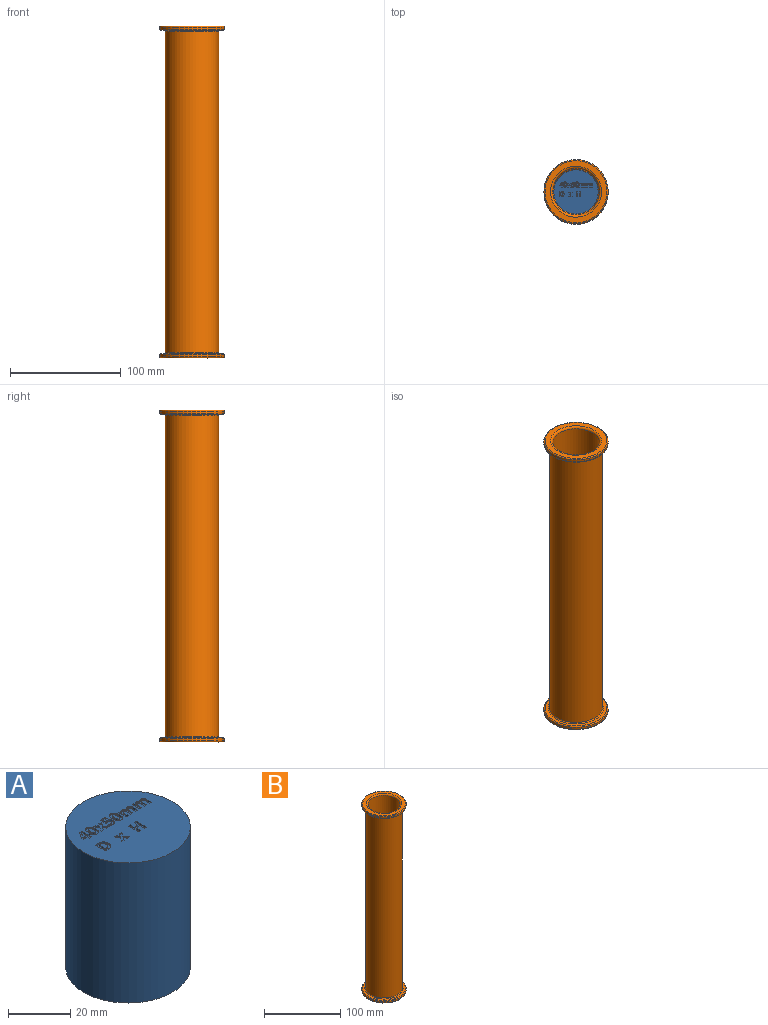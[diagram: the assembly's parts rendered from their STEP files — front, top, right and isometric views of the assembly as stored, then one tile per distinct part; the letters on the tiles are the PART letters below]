
ASSEMBLY  parts=2 mates=1
PART A: 191 faces, bbox 40x40x55 mm
  f0: plane 40x40mm, normal (0,0,1), area 1153.8mm2, adj f1,f3,f4,f5,f6,f7,f8,f9
  f1: cylinder r=20mm len=55mm, axis (0,0,-1), area 6911.5mm2, adj f0,f2
  f2: plane 40x40mm, normal (0,0,-1), area 1256.6mm2, adj f1
  f3: plane 1.7x1.12mm, normal (0.84,0.55,0), area 1mm2, adj f0,f4,f14,f15
  f4: plane 1.77x1.18mm, normal (0.83,-0.55,0), area 1.1mm2, adj f0,f3,f5,f15
  f5: plane 1.07x0.5mm, normal (0,1,0), area 0.5mm2, adj f0,f4,f6,f15
  f6: plane 1.19x0.73mm, normal (-0.85,0.52,0), area 0.7mm2, adj f0,f5,f7,f15
  f7: plane 1.19x0.73mm, normal (0.85,0.52,0), area 0.7mm2, adj f0,f6,f8,f15
  f8: plane 1.08x0.5mm, normal (0,1,0), area 0.5mm2, adj f0,f7,f9,f15
  f9: plane 1.77x1.18mm, normal (-0.83,-0.56,0), area 1.1mm2, adj f0,f8,f10,f15
  f10: plane 1.7x1.13mm, normal (-0.83,0.55,0), area 1mm2, adj f0,f9,f11,f15
  f11: plane 1.07x0.5mm, normal (0,-1,0), area 0.5mm2, adj f0,f10,f12,f15
  f12: plane 1.1x0.68mm, normal (0.85,-0.52,0), area 0.6mm2, adj f0,f11,f13,f15
  f13: plane 1.1x0.67mm, normal (-0.85,-0.52,0), area 0.6mm2, adj f0,f12,f14,f15
  f14: plane 1.07x0.5mm, normal (0,-1,0), area 0.5mm2, adj f0,f3,f13,f15
  f15: plane 3.61x3.46mm, normal (0,0,1), area 6.7mm2, adj f3,f4,f5,f6,f7,f8,f9,f10
  f16: extruded ~1.46x1.29mm, area 1.1mm2, adj f17,f27,f28,f187
  f17: extruded ~1.49x1.39mm, area 1.2mm2, adj f16,f18,f28,f187
  f18: plane 0.5x0.41mm, normal (0,-1,0), area 0.2mm2, adj f17,f19,f28,f187
  f19: plane 2.95x0.5mm, normal (-1,0,0), area 1.5mm2, adj f18,f27,f28,f187
  f20: extruded ~1.71x0.64mm, area 0.9mm2, adj f0,f21,f26,f28
  f21: extruded ~1.64x0.61mm, area 0.9mm2, adj f0,f20,f22,f28
  f22: extruded ~1.72x0.59mm, area 0.9mm2, adj f0,f21,f23,f28
  f23: plane 1.42x0.5mm, normal (0,-1,0), area 0.7mm2, adj f0,f22,f24,f28
  f24: plane 4.53x0.5mm, normal (1,0,0), area 2.3mm2, adj f0,f23,f25,f28
  f25: plane 1.28x0.5mm, normal (0,1,0), area 0.6mm2, adj f0,f24,f26,f28
  f26: extruded ~1.84x0.6mm, area 1mm2, adj f0,f20,f25,f28
  f27: plane 0.51x0.5mm, normal (0,1,0), area 0.3mm2, adj f16,f19,f28,f187
  f28: plane 4.53x3.76mm, normal (0,0,1), area 10.4mm2, adj f16,f17,f18,f19,f20,f21,f22,f23
  f29: plane 1.7x1.12mm, normal (0.84,0.55,0), area 1mm2, adj f0,f30,f40,f41
  f30: plane 1.77x1.18mm, normal (0.83,-0.55,0), area 1.1mm2, adj f0,f29,f31,f41
  f31: plane 1.07x0.5mm, normal (0,1,0), area 0.5mm2, adj f0,f30,f32,f41
  f32: plane 1.19x0.73mm, normal (-0.85,0.52,0), area 0.7mm2, adj f0,f31,f33,f41
  f33: plane 1.19x0.73mm, normal (0.85,0.52,0), area 0.7mm2, adj f0,f32,f34,f41
  f34: plane 1.08x0.5mm, normal (0,1,0), area 0.5mm2, adj f0,f33,f35,f41
  f35: plane 1.77x1.18mm, normal (-0.83,-0.56,0), area 1.1mm2, adj f0,f34,f36,f41
  f36: plane 1.7x1.13mm, normal (-0.83,0.55,0), area 1mm2, adj f0,f35,f37,f41
  f37: plane 1.07x0.5mm, normal (0,-1,0), area 0.5mm2, adj f0,f36,f38,f41
  f38: plane 1.1x0.68mm, normal (0.85,-0.52,0), area 0.6mm2, adj f0,f37,f39,f41
  f39: plane 1.1x0.67mm, normal (-0.85,-0.52,0), area 0.6mm2, adj f0,f38,f40,f41
  f40: plane 1.07x0.5mm, normal (0,-1,0), area 0.5mm2, adj f0,f29,f39,f41
  f41: plane 3.61x3.46mm, normal (0,0,1), area 6.7mm2, adj f29,f30,f31,f32,f33,f34,f35,f36
  f42: plane 0.95x0.5mm, normal (0,1,0), area 0.5mm2, adj f0,f43,f69,f70
  f43: plane 1.74x0.5mm, normal (-1,0,0), area 0.9mm2, adj f0,f42,f44,f70
  f44: extruded ~0.79x0.5mm, area 0.4mm2, adj f0,f43,f45,f70
  f45: extruded ~0.52x0.5mm, area 0.3mm2, adj f0,f44,f46,f70
  f46: extruded ~0.5x0.4mm, area 0.2mm2, adj f0,f45,f47,f70
  f47: extruded ~0.56x0.5mm, area 0.3mm2, adj f0,f46,f48,f70
  f48: plane 2.02x0.5mm, normal (1,0,0), area 1mm2, adj f0,f47,f49,f70
  f49: plane 0.95x0.5mm, normal (0,1,0), area 0.5mm2, adj f0,f48,f50,f70
  f50: plane 2.26x0.5mm, normal (-1,0,0), area 1.1mm2, adj f0,f49,f51,f70
  f51: extruded ~0.97x0.5mm, area 0.5mm2, adj f0,f50,f52,f70
  f52: extruded ~0.89x0.5mm, area 0.5mm2, adj f0,f51,f53,f70
  f53: extruded ~0.61x0.5mm, area 0.3mm2, adj f0,f52,f54,f70
  f54: extruded ~0.5x0.41mm, area 0.3mm2, adj f0,f53,f55,f70
  f55: plane 0.5x0.08mm, normal (0,-1,0), area 0mm2, adj f0,f54,f56,f70
  f56: extruded ~1.05x0.51mm, area 0.6mm2, adj f0,f55,f57,f70
  f57: extruded ~0.6x0.5mm, area 0.3mm2, adj f0,f56,f58,f70
  f58: extruded ~0.5x0.4mm, area 0.3mm2, adj f0,f57,f59,f70
  f59: plane 0.5x0.05mm, normal (0,-1,0), area 0mm2, adj f0,f58,f60,f70
  f60: plane 0.5x0.44mm, normal (-0.96,-0.28,0), area 0.2mm2, adj f0,f59,f61,f70
  f61: plane 0.72x0.5mm, normal (0,-1,0), area 0.4mm2, adj f0,f60,f62,f70
  f62: plane 3.46x0.5mm, normal (1,0,0), area 1.7mm2, adj f0,f61,f63,f70
  f63: plane 0.95x0.5mm, normal (0,1,0), area 0.5mm2, adj f0,f62,f64,f70
  f64: plane 1.63x0.5mm, normal (-1,0,0), area 0.8mm2, adj f0,f63,f65,f70
  f65: extruded ~0.88x0.5mm, area 0.5mm2, adj f0,f64,f66,f70
  f66: extruded ~0.53x0.5mm, area 0.3mm2, adj f0,f65,f67,f70
  f67: extruded ~0.5x0.4mm, area 0.2mm2, adj f0,f66,f68,f70
  f68: extruded ~0.56x0.5mm, area 0.3mm2, adj f0,f67,f69,f70
  f69: plane 2.02x0.5mm, normal (1,0,0), area 1mm2, adj f0,f42,f68,f70
  f70: plane 5.26x3.53mm, normal (0,0,1), area 11.4mm2, adj f42,f43,f44,f45,f46,f47,f48,f49
  f71: plane 0.95x0.5mm, normal (0,1,0), area 0.5mm2, adj f0,f72,f98,f99
  f72: plane 1.74x0.5mm, normal (-1,0,0), area 0.9mm2, adj f0,f71,f73,f99
  f73: extruded ~0.79x0.5mm, area 0.4mm2, adj f0,f72,f74,f99
  f74: extruded ~0.52x0.5mm, area 0.3mm2, adj f0,f73,f75,f99
  f75: extruded ~0.5x0.4mm, area 0.2mm2, adj f0,f74,f76,f99
  f76: extruded ~0.56x0.5mm, area 0.3mm2, adj f0,f75,f77,f99
  f77: plane 2.02x0.5mm, normal (1,0,0), area 1mm2, adj f0,f76,f78,f99
  f78: plane 0.95x0.5mm, normal (0,1,0), area 0.5mm2, adj f0,f77,f79,f99
  f79: plane 2.26x0.5mm, normal (-1,0,0), area 1.1mm2, adj f0,f78,f80,f99
  f80: extruded ~0.97x0.5mm, area 0.5mm2, adj f0,f79,f81,f99
  f81: extruded ~0.89x0.5mm, area 0.5mm2, adj f0,f80,f82,f99
  f82: extruded ~0.61x0.5mm, area 0.3mm2, adj f0,f81,f83,f99
  f83: extruded ~0.5x0.41mm, area 0.3mm2, adj f0,f82,f84,f99
  f84: plane 0.5x0.08mm, normal (0,-1,0), area 0mm2, adj f0,f83,f85,f99
  f85: extruded ~1.05x0.51mm, area 0.6mm2, adj f0,f84,f86,f99
  f86: extruded ~0.6x0.5mm, area 0.3mm2, adj f0,f85,f87,f99
  f87: extruded ~0.5x0.4mm, area 0.3mm2, adj f0,f86,f88,f99
  f88: plane 0.5x0.05mm, normal (0,-1,0), area 0mm2, adj f0,f87,f89,f99
  f89: plane 0.5x0.44mm, normal (-0.96,-0.28,0), area 0.2mm2, adj f0,f88,f90,f99
  f90: plane 0.72x0.5mm, normal (0,-1,0), area 0.4mm2, adj f0,f89,f91,f99
  f91: plane 3.46x0.5mm, normal (1,0,0), area 1.7mm2, adj f0,f90,f92,f99
  f92: plane 0.95x0.5mm, normal (0,1,0), area 0.5mm2, adj f0,f91,f93,f99
  f93: plane 1.63x0.5mm, normal (-1,0,0), area 0.8mm2, adj f0,f92,f94,f99
  f94: extruded ~0.88x0.5mm, area 0.5mm2, adj f0,f93,f95,f99
  f95: extruded ~0.53x0.5mm, area 0.3mm2, adj f0,f94,f96,f99
  f96: extruded ~0.5x0.4mm, area 0.2mm2, adj f0,f95,f97,f99
  f97: extruded ~0.56x0.5mm, area 0.3mm2, adj f0,f96,f98,f99
  f98: plane 2.02x0.5mm, normal (1,0,0), area 1mm2, adj f0,f71,f97,f99
  f99: plane 5.26x3.53mm, normal (0,0,1), area 11.4mm2, adj f71,f72,f73,f74,f75,f76,f77,f78
  f100: extruded ~1.05x0.5mm, area 0.6mm2, adj f0,f101,f119,f120
  f101: extruded ~0.5x0.47mm, area 0.2mm2, adj f0,f100,f102,f120
  f102: plane 0.5x0.11mm, normal (0.2,-0.98,0), area 0.1mm2, adj f0,f101,f103,f120
  f103: plane 0.89x0.5mm, normal (-1,0.09,0), area 0.4mm2, adj f0,f102,f104,f120
  f104: plane 1.62x0.5mm, normal (0,1,0), area 0.8mm2, adj f0,f103,f105,f120
  f105: plane 0.81x0.5mm, normal (-1,0,0), area 0.4mm2, adj f0,f104,f106,f120
  f106: plane 2.46x0.5mm, normal (0,-1,0), area 1.2mm2, adj f0,f105,f107,f120
  f107: plane 2.31x0.5mm, normal (1,-0.07,0), area 1.2mm2, adj f0,f106,f108,f120
  f108: plane 0.5x0.38mm, normal (0.47,0.88,0), area 0.2mm2, adj f0,f107,f109,f120
  f109: extruded ~0.5x0.32mm, area 0.2mm2, adj f0,f108,f110,f120
  f110: extruded ~0.5x0.36mm, area 0.2mm2, adj f0,f109,f111,f120
  f111: extruded ~0.91x0.69mm, area 0.6mm2, adj f0,f110,f112,f120
  f112: extruded ~0.88x0.72mm, area 0.6mm2, adj f0,f111,f113,f120
  f113: extruded ~0.62x0.5mm, area 0.3mm2, adj f0,f112,f114,f120
  f114: extruded ~0.57x0.5mm, area 0.3mm2, adj f0,f113,f115,f120
  f115: plane 0.83x0.5mm, normal (1,0,0), area 0.4mm2, adj f0,f114,f116,f120
  f116: extruded ~1.22x0.5mm, area 0.6mm2, adj f0,f115,f117,f120
  f117: extruded ~1.34x0.5mm, area 0.7mm2, adj f0,f116,f118,f120
  f118: extruded ~1.17x0.5mm, area 0.6mm2, adj f0,f117,f119,f120
  f119: extruded ~1.01x0.5mm, area 0.6mm2, adj f0,f100,f118,f120
  f120: plane 4.59x3.03mm, normal (0,0,1), area 8.1mm2, adj f100,f101,f102,f103,f104,f105,f106,f107
  f121: extruded ~1.19x0.5mm, area 0.6mm2, adj f122,f136,f137,f188
  f122: extruded ~1.2x0.5mm, area 0.6mm2, adj f121,f123,f137,f188
  f123: extruded ~0.5x0.48mm, area 0.3mm2, adj f122,f124,f137,f188
  f124: extruded ~0.5x0.48mm, area 0.3mm2, adj f123,f125,f137,f188
  f125: extruded ~1.2x0.5mm, area 0.6mm2, adj f124,f126,f137,f188
  f126: extruded ~1.19x0.5mm, area 0.6mm2, adj f125,f127,f137,f188
  f127: extruded ~0.5x0.48mm, area 0.3mm2, adj f126,f136,f137,f188
  f128: extruded ~1.76x0.5mm, area 0.9mm2, adj f0,f129,f135,f137
  f129: extruded ~1.74x0.5mm, area 0.9mm2, adj f0,f128,f130,f137
  f130: extruded ~1.19x0.6mm, area 0.7mm2, adj f0,f129,f131,f137
  f131: extruded ~1.19x0.57mm, area 0.7mm2, adj f0,f130,f132,f137
  f132: extruded ~1.77x0.5mm, area 0.9mm2, adj f0,f131,f133,f137
  f133: extruded ~1.74x0.5mm, area 0.9mm2, adj f0,f132,f134,f137
  f134: extruded ~1.18x0.59mm, area 0.7mm2, adj f0,f133,f135,f137
  f135: extruded ~1.2x0.57mm, area 0.7mm2, adj f0,f128,f134,f137
  f136: extruded ~0.5x0.49mm, area 0.3mm2, adj f121,f127,f137,f188
  f137: plane 4.66x3.17mm, normal (0,0,1), area 9mm2, adj f121,f122,f123,f124,f125,f126,f127,f128
  f138: extruded ~1.19x0.5mm, area 0.6mm2, adj f139,f153,f154,f189
  f139: extruded ~1.2x0.5mm, area 0.6mm2, adj f138,f140,f154,f189
  f140: extruded ~0.5x0.48mm, area 0.3mm2, adj f139,f141,f154,f189
  f141: extruded ~0.5x0.48mm, area 0.3mm2, adj f140,f142,f154,f189
  f142: extruded ~1.2x0.5mm, area 0.6mm2, adj f141,f143,f154,f189
  f143: extruded ~1.19x0.5mm, area 0.6mm2, adj f142,f144,f154,f189
  f144: extruded ~0.5x0.48mm, area 0.3mm2, adj f143,f153,f154,f189
  f145: extruded ~1.76x0.5mm, area 0.9mm2, adj f0,f146,f152,f154
  f146: extruded ~1.74x0.5mm, area 0.9mm2, adj f0,f145,f147,f154
  f147: extruded ~1.19x0.6mm, area 0.7mm2, adj f0,f146,f148,f154
  f148: extruded ~1.19x0.57mm, area 0.7mm2, adj f0,f147,f149,f154
  f149: extruded ~1.77x0.5mm, area 0.9mm2, adj f0,f148,f150,f154
  f150: extruded ~1.74x0.5mm, area 0.9mm2, adj f0,f149,f151,f154
  f151: extruded ~1.18x0.59mm, area 0.7mm2, adj f0,f150,f152,f154
  f152: extruded ~1.2x0.57mm, area 0.7mm2, adj f0,f145,f151,f154
  f153: extruded ~0.5x0.49mm, area 0.3mm2, adj f138,f144,f154,f189
  f154: plane 4.66x3.17mm, normal (0,0,1), area 9mm2, adj f138,f139,f140,f141,f142,f143,f144,f145
  f155: plane 0.77x0.5mm, normal (1,0,0), area 0.4mm2, adj f156,f172,f173,f190
  f156: plane 1.09x0.5mm, normal (0,-1,0), area 0.5mm2, adj f155,f157,f173,f190
  f157: plane 1.26x0.83mm, normal (-0.83,0.55,0), area 0.8mm2, adj f156,f158,f173,f190
  f158: extruded ~0.5x0.5mm, area 0.3mm2, adj f157,f159,f173,f190
  f159: plane 0.5x0.02mm, normal (0,1,0), area 0mm2, adj f158,f160,f173,f190
  f160: extruded ~0.5x0.43mm, area 0.2mm2, adj f159,f172,f173,f190
  f161: plane 0.55x0.5mm, normal (0,1,0), area 0.3mm2, adj f0,f162,f171,f173
  f162: plane 0.74x0.5mm, normal (-1,0,0), area 0.4mm2, adj f0,f161,f163,f173
  f163: plane 0.55x0.5mm, normal (0,-1,0), area 0.3mm2, adj f0,f162,f164,f173
  f164: plane 2.85x0.5mm, normal (-1,0,0), area 1.4mm2, adj f0,f163,f165,f173
  f165: plane 0.88x0.5mm, normal (0,-1,0), area 0.4mm2, adj f0,f164,f166,f173
  f166: plane 2.93x1.99mm, normal (0.83,-0.56,0), area 1.8mm2, adj f0,f165,f167,f173
  f167: plane 0.67x0.5mm, normal (1,0,0), area 0.3mm2, adj f0,f166,f168,f173
  f168: plane 1.93x0.5mm, normal (0,1,0), area 1mm2, adj f0,f167,f169,f173
  f169: plane 0.94x0.5mm, normal (1,0,0), area 0.5mm2, adj f0,f168,f170,f173
  f170: plane 0.94x0.5mm, normal (0,1,0), area 0.5mm2, adj f0,f169,f171,f173
  f171: plane 0.94x0.5mm, normal (-1,0,0), area 0.5mm2, adj f0,f161,f170,f173
  f172: extruded ~0.56x0.5mm, area 0.3mm2, adj f155,f160,f173,f190
  f173: plane 4.53x3.41mm, normal (0,0,1), area 7.8mm2, adj f155,f156,f157,f158,f159,f160,f161,f162
  f174: plane 0.96x0.5mm, normal (0,1,0), area 0.5mm2, adj f0,f175,f185,f186
  f175: plane 4.53x0.5mm, normal (-1,0,0), area 2.3mm2, adj f0,f174,f176,f186
  f176: plane 0.96x0.5mm, normal (0,-1,0), area 0.5mm2, adj f0,f175,f177,f186
  f177: plane 1.78x0.5mm, normal (1,0,0), area 0.9mm2, adj f0,f176,f178,f186
  f178: plane 1.79x0.5mm, normal (0,-1,0), area 0.9mm2, adj f0,f177,f179,f186
  f179: plane 1.78x0.5mm, normal (-1,0,0), area 0.9mm2, adj f0,f178,f180,f186
  f180: plane 0.96x0.5mm, normal (0,-1,0), area 0.5mm2, adj f0,f179,f181,f186
  f181: plane 4.53x0.5mm, normal (1,0,0), area 2.3mm2, adj f0,f180,f182,f186
  f182: plane 0.96x0.5mm, normal (0,1,0), area 0.5mm2, adj f0,f181,f183,f186
  f183: plane 1.96x0.5mm, normal (-1,0,0), area 1mm2, adj f0,f182,f184,f186
  f184: plane 1.79x0.5mm, normal (0,1,0), area 0.9mm2, adj f0,f183,f185,f186
  f185: plane 1.96x0.5mm, normal (1,0,0), area 1mm2, adj f0,f174,f184,f186
  f186: plane 4.53x3.71mm, normal (0,0,1), area 10.1mm2, adj f174,f175,f176,f177,f178,f179,f180,f181
  f187: plane 2.95x1.8mm, normal (0,0,1), area 4.6mm2, adj f16,f17,f18,f19,f27
  f188: plane 3.12x1.26mm, normal (0,0,1), area 3.3mm2, adj f121,f122,f123,f124,f125,f126,f127,f136
  f189: plane 3.12x1.26mm, normal (0,0,1), area 3.3mm2, adj f138,f139,f140,f141,f142,f143,f144,f153
  f190: plane 1.75x1.13mm, normal (0,0,1), area 0.9mm2, adj f155,f156,f157,f158,f159,f160,f172
PART B: 17 faces, bbox 62.8x62.8x300 mm
  f0: cylinder r=29mm len=58mm, axis (0,0,-1), area 364.4mm2, adj f1,f16
  f1: torus R=28mm, axis (0,0,-1), area 282.6mm2, adj f0,f2
  f2: plane 56x56mm, normal (0,0,-1), area 499.5mm2, adj f1,f3
  f3: torus R=25mm, axis (0,0,-1), area 240.5mm2, adj f2,f4
  f4: cylinder r=24mm len=290mm, axis (0,0,-1), area 43731mm2, adj f3,f5
  f5: torus R=25mm, axis (0,0,-1), area 240.5mm2, adj f4,f6
  f6: plane 56x56mm, normal (0,0,1), area 499.5mm2, adj f5,f7
  f7: torus R=28mm, axis (0,0,-1), area 282.6mm2, adj f6,f8
  f8: cylinder r=29mm len=58mm, axis (0,0,-1), area 364.4mm2, adj f7,f9
  f9: torus R=28mm, axis (0,0,-1), area 282.6mm2, adj f8,f10
  f10: revolved ~56x56mm, area 2466.1mm2, adj f9
  f11: plane 38x38mm, normal (0,0,1), area 1134.1mm2, adj f12
  f12: torus R=19mm, axis (0,0,-1), area 400.2mm2, adj f11,f13
  f13: cylinder r=21mm len=292mm, axis (0,0,-1), area 38528.5mm2, adj f12,f14
  f14: torus R=23mm, axis (0,0,-1), area 428.9mm2, adj f13,f15
  f15: plane 56x56mm, normal (0,0,1), area 801.1mm2, adj f14,f16
  f16: torus R=28mm, axis (0,0,-1), area 282.6mm2, adj f0,f15
PLACE A rot(axis=(0.88,0.47,-0.08),0deg) t=(25.99,-35.82,11.41)mm
PLACE B rot(axis=(0.88,0.47,-0.08),0deg) t=(43.99,-35.82,-125.03)mm
MATE slider A.f1 <-> B.f0  axis (0,0,-1) through (25.99,-35.82,11.41)mm
